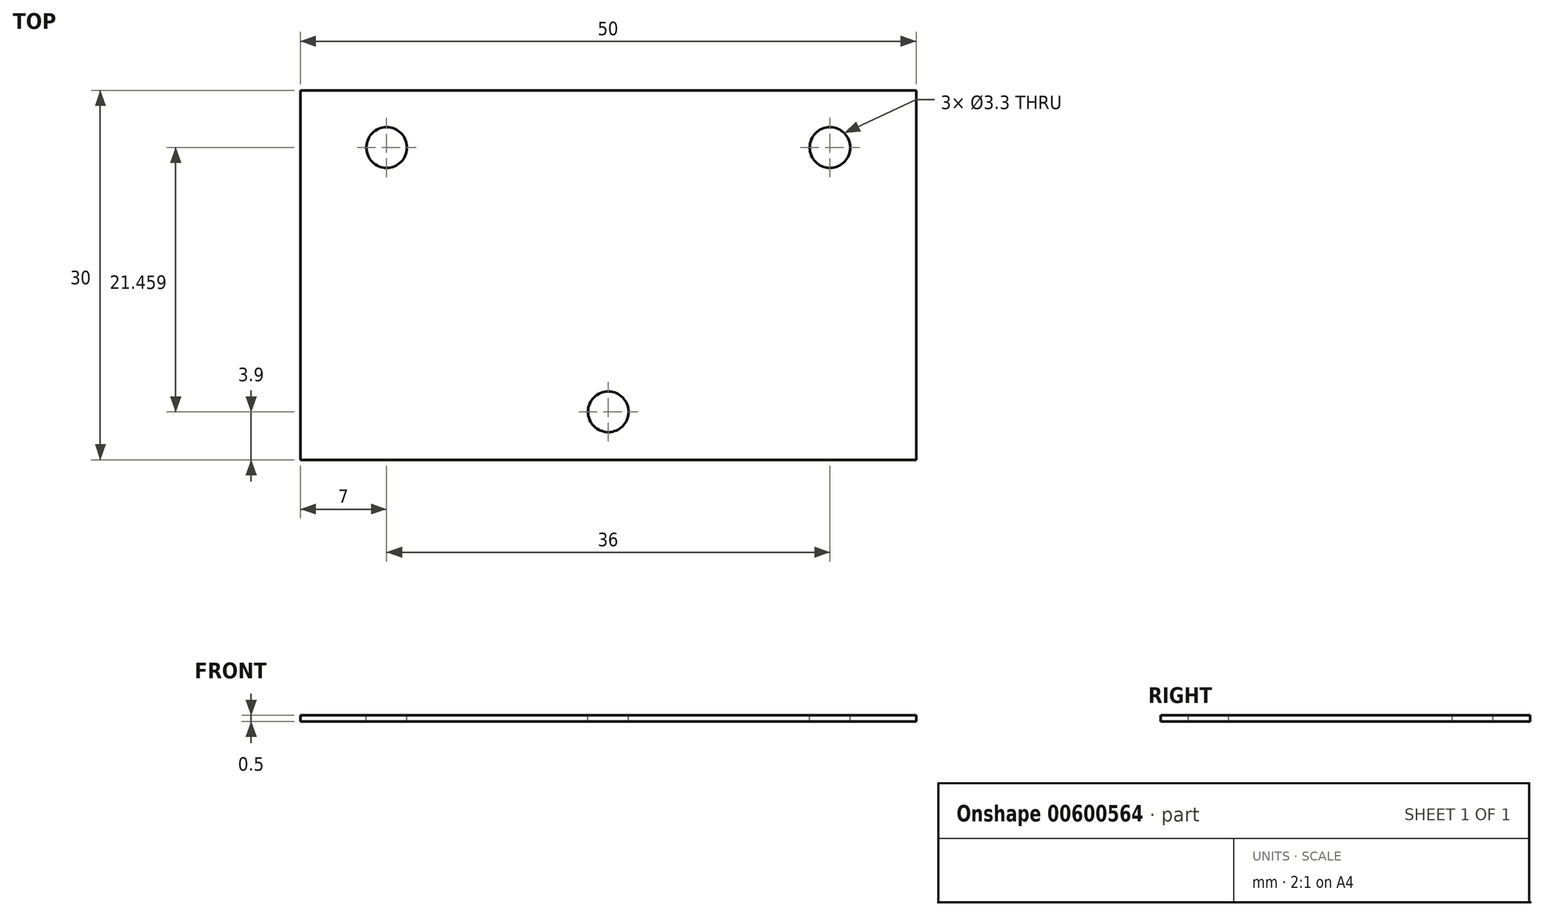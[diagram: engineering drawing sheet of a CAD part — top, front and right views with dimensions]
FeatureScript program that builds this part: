
annotation { "Feature Type Name" : "Feature", "Feature Type Description" : "" }
export const myFeature = defineFeature(function(context is Context, id is Id, definition is map)
    precondition{}
    {
        {
            var Q0;
            Q0=qCreatedBy(makeId("Top.planeOp"),FACE);
            var sketch = newSketch(context, id + "F0", { "sketchPlane" : qUnion([Q0])});
            skLineSegment(sketch, "E0.bottom", {"start": v(-25, 4) * mm, "end": v(25, 4) * mm});
            skLineSegment(sketch, "E0.top", {"start": v(-25, -4) * mm, "end": v(25, -4) * mm});
            skLineSegment(sketch, "E0.left", {"start": v(-25, 4) * mm, "end": v(-25, -4) * mm});
            skLineSegment(sketch, "E0.right", {"start": v(25, 4) * mm, "end": v(25, -4) * mm});
            skPoint(sketch, "E0.middle", {"position": v(0, 0) * mm});
            skSolve(sketch);
        }
        {
            var Q0;
            Q0=makeQuery(id+"F0.imprint","IMPRINT",FACE,{"disambiguationData":[TD([[makeQuery(id+"F0.imprint","IMPRINT",EDGE,{"derivedFrom":sQuery(id+"F0.wireOp",EDGE,"E0.bottom")}),-1.0]])]});
            extrude(context, id + "F1", {"entities" : qUnion([Q0]), "depth" : 4 * mm, "offsetDistance" : 25 * mm});
        }
        {
            var Q0;
            Q0=makeQuery(id+"F1.opExtrude","CAP_FACE",FACE,{"disambiguationData":[OSD([sQuery(id+"F0.wireOp",EDGE,"E0.bottom"),sQuery(id+"F0.wireOp",EDGE,"E0.top"),sQuery(id+"F0.wireOp",EDGE,"E0.left"),sQuery(id+"F0.wireOp",EDGE,"E0.right")])],"isStart":false});
            var sketch = newSketch(context, id + "F2", { "sketchPlane" : qUnion([Q0])});
            skLineSegment(sketch, "E1", {"start": v(0, -4) * mm, "end": v(0, -2.5) * mm});
            skPoint(sketch, "E1.endSnap0", {"position": v(0, -4) * mm});
            skLineSegment(sketch, "E2", {"start": v(0, 4) * mm, "end": v(0, 0) * mm});
            skLineSegment(sketch, "E3", {"start": v(0, 0) * mm, "end": v(0, 4) * mm});
            skLineSegment(sketch, "E4", {"start": v(25, 4) * mm, "end": v(18.35, 4) * mm});
            skLineSegment(sketch, "E5", {"start": v(18.35, 4) * mm, "end": v(18.35, 2.5) * mm});
            skLineSegment(sketch, "E6", {"start": v(-25, 4) * mm, "end": v(-18.35, 4) * mm});
            skLineSegment(sketch, "E7", {"start": v(-18.35, 4) * mm, "end": v(-18.35, 2.5) * mm});
            skSolve(sketch);
        }
        {
            var Q0;
            Q0=makeQuery(id+"F1.opExtrude","SWEPT_FACE",FACE,{"disambiguationData":[OSD([sQuery(id+"F0.wireOp",EDGE,"E0.top")])]});
            extrude(context, id + "F3", {"entities" : qUnion([Q0]), "operationType" : NewBodyOperationType.ADD, "depth" : 5 * mm, "offsetDistance" : 25 * mm});
        }
        {
            var Q0;
            Q0=makeQuery(id+"F1.opExtrude","SWEPT_FACE",FACE,{"disambiguationData":[OSD([sQuery(id+"F0.wireOp",EDGE,"E0.bottom")])]});
            extrude(context, id + "F4", {"entities" : qUnion([Q0]), "operationType" : NewBodyOperationType.ADD, "depth" : 5 * mm, "offsetDistance" : 25 * mm});
        }
        {
            var Q0;
            Q0=sQuery(id+"F2.wireOp",VERTEX,"E1.endSnap0");
            var Q1;
            Q1=makeQuery(id+"F1.opExtrude","SWEPT_BODY",BODY,{"disambiguationData":[OSD([sQuery(id+"F0.wireOp",EDGE,"E0.bottom"),sQuery(id+"F0.wireOp",EDGE,"E0.top"),sQuery(id+"F0.wireOp",EDGE,"E0.left"),sQuery(id+"F0.wireOp",EDGE,"E0.right")])]});
            hole(context, id + "F5", {"style" : HoleStyle.C_BORE, "endStyle" : HoleEndStyle.THROUGH, "holeDiameter" : 3.3 * mm, "cBoreDiameter" : 6.5 * mm, "cBoreDepth" : 0 * mm, "majorDiameter" : 5 * mm, "isTappedThrough" : true, "tappedDepth" : 12 * mm, "tapClearance" : 3, "locations" : qUnion([Q0]), "scope" : qUnion([Q1])});
        }
        {
            var Q0;
            Q0=makeQuery(id+"F3.opExtrude","CAP_FACE",FACE,{"disambiguationData":[OSD([sQuery(id+"F0.wireOp",EDGE,"E0.top")])],"isStart":false});
            extrude(context, id + "F6", {"entities" : qUnion([Q0]), "operationType" : NewBodyOperationType.REMOVE, "oppositeDirection" : true, "depth" : 1.1 * mm, "offsetDistance" : 25 * mm});
        }
        {
            var Q0;
            Q0=makeQuery(id+"F4.opExtrude","CAP_FACE",FACE,{"disambiguationData":[OSD([sQuery(id+"F0.wireOp",EDGE,"E0.bottom")])],"isStart":false});
            extrude(context, id + "F7", {"entities" : qUnion([Q0]), "operationType" : NewBodyOperationType.ADD, "depth" : 4.4 * mm, "offsetDistance" : 25 * mm});
        }
        {
            var Q0;
            {var subQ0=sQuery(id+"F0.wireOp",EDGE,"E0.bottom");var subQ1=makeQuery(id+"F1.opExtrude","CAP_EDGE",EDGE,{"disambiguationData":[OSD([subQ0])],"isStart":true});var subQ2=sQuery(id+"F0.wireOp",EDGE,"E0.top");Q0=makeQuery(id+"F7.boolean.opBoolean","MERGE",FACE,{"derivedFrom":[makeQuery(id+"F4.boolean.opBoolean","MERGE",FACE,{"derivedFrom":[makeQuery(id+"F3.boolean.opBoolean","MERGE",FACE,{"derivedFrom":[makeQuery(id+"F1.opExtrude","CAP_FACE",FACE,{"disambiguationData":[OSD([subQ0,subQ2,sQuery(id+"F0.wireOp",EDGE,"E0.left"),sQuery(id+"F0.wireOp",EDGE,"E0.right")])],"isStart":true}),makeQuery(id+"F3.opExtrude","SWEPT_FACE",FACE,{"disambiguationData":[OSD([subQ2]),TDD([makeQuery(id+"F1.opExtrude","CAP_EDGE",EDGE,{"disambiguationData":[OSD([subQ2])],"isStart":true})])]})]}),makeQuery(id+"F4.opExtrude","SWEPT_FACE",FACE,{"disambiguationData":[OSD([subQ0]),TDD([subQ1])]})]}),makeQuery(id+"F7.opExtrude","SWEPT_FACE",FACE,{"disambiguationData":[OSD([subQ0]),TDD([makeQuery(id+"F4.opExtrude","CAP_EDGE",EDGE,{"disambiguationData":[OSD([subQ0]),TDD([subQ1])],"isStart":false})])]})]});}
            extrude(context, id + "F8", {"entities" : qUnion([Q0]), "operationType" : NewBodyOperationType.REMOVE, "oppositeDirection" : true, "depth" : 3.5 * mm, "offsetDistance" : 25 * mm});
        }
        {
            var Q0;
            Q0=makeQuery(id+"F7.opExtrude","CAP_FACE",FACE,{"disambiguationData":[OSD([sQuery(id+"F0.wireOp",EDGE,"E0.bottom")])],"isStart":false});
            extrude(context, id + "F9", {"entities" : qUnion([Q0]), "operationType" : NewBodyOperationType.ADD, "depth" : 8.7 * mm, "offsetDistance" : 25 * mm});
        }
        {
            var Q0;
            {var subQ0=sQuery(id+"F0.wireOp",EDGE,"E0.bottom");var subQ1=makeQuery(id+"F1.opExtrude","CAP_EDGE",EDGE,{"disambiguationData":[OSD([subQ0])],"isStart":false});var subQ2=makeQuery(id+"F4.opExtrude","CAP_EDGE",EDGE,{"disambiguationData":[OSD([subQ0]),TDD([subQ1])],"isStart":false});var subQ3=sQuery(id+"F0.wireOp",EDGE,"E0.top");Q0=makeQuery(id+"F9.boolean.opBoolean","MERGE",FACE,{"derivedFrom":[makeQuery(id+"F7.boolean.opBoolean","MERGE",FACE,{"derivedFrom":[makeQuery(id+"F4.boolean.opBoolean","MERGE",FACE,{"derivedFrom":[makeQuery(id+"F3.boolean.opBoolean","MERGE",FACE,{"derivedFrom":[makeQuery(id+"F1.opExtrude","CAP_FACE",FACE,{"disambiguationData":[OSD([subQ0,subQ3,sQuery(id+"F0.wireOp",EDGE,"E0.left"),sQuery(id+"F0.wireOp",EDGE,"E0.right")])],"isStart":false}),makeQuery(id+"F3.opExtrude","SWEPT_FACE",FACE,{"disambiguationData":[OSD([subQ3]),TDD([makeQuery(id+"F1.opExtrude","CAP_EDGE",EDGE,{"disambiguationData":[OSD([subQ3])],"isStart":false})])]})]}),makeQuery(id+"F4.opExtrude","SWEPT_FACE",FACE,{"disambiguationData":[OSD([subQ0]),TDD([subQ1])]})]}),makeQuery(id+"F7.opExtrude","SWEPT_FACE",FACE,{"disambiguationData":[OSD([subQ0]),TDD([subQ2])]})]}),makeQuery(id+"F9.opExtrude","SWEPT_FACE",FACE,{"disambiguationData":[OSD([subQ0]),TDD([makeQuery(id+"F7.opExtrude","CAP_EDGE",EDGE,{"disambiguationData":[OSD([subQ0]),TDD([subQ2])],"isStart":false})])]})]});}
            var sketch = newSketch(context, id + "F10", { "sketchPlane" : qUnion([Q0])});
            skLineSegment(sketch, "E8", {"start": v(-25, 12.82) * mm, "end": v(25, 12.82) * mm});
            skLineSegment(sketch, "E9", {"start": v(0, 12.82) * mm, "end": v(0, 22.1) * mm});
            skLineSegment(sketch, "E10", {"start": v(0, 22.1) * mm, "end": v(0, 17.46) * mm});
            skLineSegment(sketch, "E11", {"start": v(0, 17.46) * mm, "end": v(-18, 17.46) * mm});
            skLineSegment(sketch, "E12", {"start": v(0, 17.46) * mm, "end": v(18, 17.46) * mm});
            skPoint(sketch, "E13", {"position": v(0, -4) * mm});
            skSolve(sketch);
        }
        {
            var Q0;
            Q0=sQuery(id+"F10.wireOp",VERTEX,"E11.end");
            var Q1;
            Q1=sQuery(id+"F10.wireOp",VERTEX,"E12.end");
            var Q2;
            Q2=makeQuery(id+"F1.opExtrude","SWEPT_BODY",BODY,{"disambiguationData":[OSD([sQuery(id+"F0.wireOp",EDGE,"E0.bottom"),sQuery(id+"F0.wireOp",EDGE,"E0.top"),sQuery(id+"F0.wireOp",EDGE,"E0.left"),sQuery(id+"F0.wireOp",EDGE,"E0.right")])]});
            hole(context, id + "F11", {"style" : HoleStyle.C_BORE, "endStyle" : HoleEndStyle.THROUGH, "holeDiameter" : 3.3 * mm, "cBoreDiameter" : 6.5 * mm, "cBoreDepth" : 0 * mm, "majorDiameter" : 5 * mm, "isTappedThrough" : true, "tappedDepth" : 12 * mm, "tapClearance" : 3, "locations" : qUnion([Q0, Q1]), "scope" : qUnion([Q2])});
        }
    });
